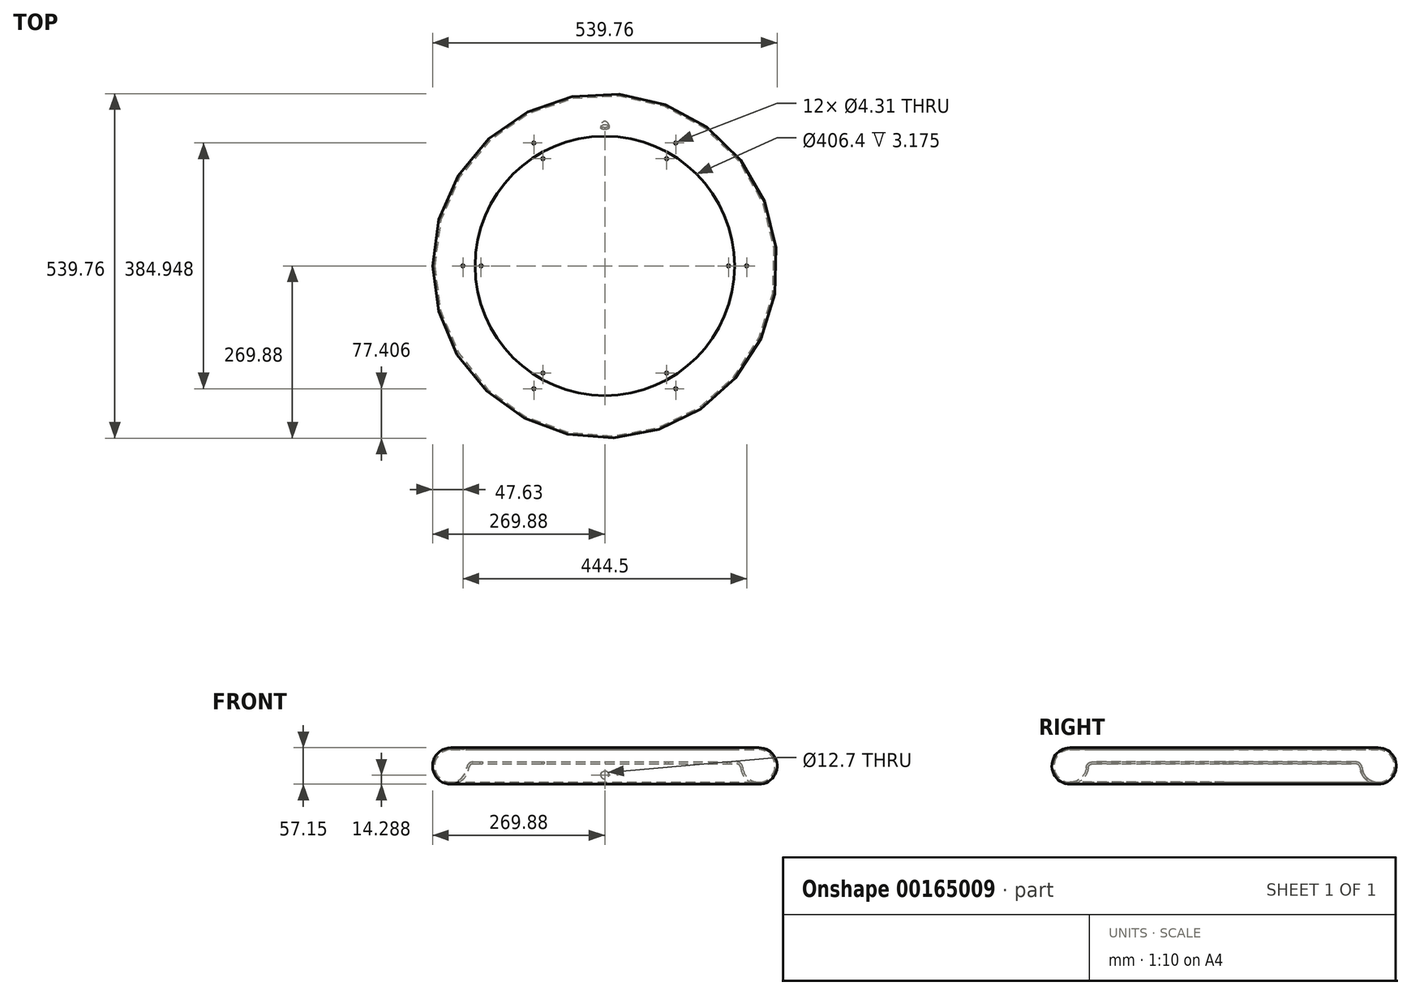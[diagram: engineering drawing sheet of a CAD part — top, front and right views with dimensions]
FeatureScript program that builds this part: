
annotation { "Feature Type Name" : "Feature", "Feature Type Description" : "" }
export const myFeature = defineFeature(function(context is Context, id is Id, definition is map)
    precondition{}
    {
        {
            var Q0;
            Q0=qCreatedBy(makeId("Front.planeOp"),FACE);
            var sketch = newSketch(context, id + "F0", { "sketchPlane" : qUnion([Q0])});
            skArc(sketch, "E0", {"start": v(212.84, -5.77) * mm, "mid": v(210.8, -1.66) * mm, "end": v(206.52, 0) * mm});
            skArc(sketch, "E1", {"start": v(216, -5.48) * mm, "mid": v(212.94, 0.68) * mm, "end": v(206.52, 3.17) * mm});
            skArc(sketch, "E2", {"start": v(212.84, -5.77) * mm, "mid": v(262.4, -22.44) * mm, "end": v(241.3, 25.4) * mm});
            skArc(sketch, "E3", {"start": v(216, -5.48) * mm, "mid": v(260.06, -20.3) * mm, "end": v(241.3, 22.23) * mm});
            skLineSegment(sketch, "E4.bottom", {"start": v(0, 0) * mm, "end": v(206.52, 0) * mm});
            skLineSegment(sketch, "E4.top", {"start": v(0, 3.18) * mm, "end": v(206.52, 3.18) * mm});
            skLineSegment(sketch, "E4.left", {"start": v(0, 0) * mm, "end": v(0, 3.18) * mm});
            skLineSegment(sketch, "E5", {"start": v(241.3, 22.23) * mm, "end": v(203.2, 22.23) * mm});
            skLineSegment(sketch, "E6", {"start": v(203.2, 22.23) * mm, "end": v(203.2, 25.4) * mm});
            skLineSegment(sketch, "E7", {"start": v(203.2, 25.4) * mm, "end": v(241.3, 25.4) * mm});
            skLineSegment(sketch, "E8", {"start": v(0, 3.18) * mm, "end": v(0, 22.23) * mm, "construction": true});
            skLineSegment(sketch, "E9", {"start": v(0, 22.23) * mm, "end": v(203.2, 22.23) * mm, "construction": true});
            skLineSegment(sketch, "E10", {"start": v(241.3, 25.4) * mm, "end": v(241.3, 69.85) * mm, "construction": true});
            skArc(sketch, "E11", {"start": v(212.87, -6.35) * mm, "mid": v(212.86, -6.06) * mm, "end": v(212.84, -5.77) * mm, "construction": true});
            skLineSegment(sketch, "E12", {"start": v(0, 0) * mm, "end": v(0, -6.35) * mm, "construction": true});
            skLineSegment(sketch, "E13", {"start": v(0, -6.35) * mm, "end": v(212.87, -6.35) * mm, "construction": true});
            skSolve(sketch);
        }
        {
            var Q0;
            Q0=qCreatedBy(makeId("Top.planeOp"),FACE);
            var sketch = newSketch(context, id + "F1", { "sketchPlane" : qUnion([Q0])});
            skCircle(sketch, "E14", {"center": v(0, 0) * mm, "radius": 25.4 * mm});
            skSolve(sketch);
        }
        {
            var Q0;
            Q0=qSketchRegion(id+"F0",true);
            var Q1;
            Q1=sQuery(id+"F1.wireOp",EDGE,"E14");
            revolve(context, id + "F2", {"entities" : qUnion([Q0]), "axis" : qUnion([Q1]), "revolveType" : RevolveType.FULL});
        }
        {
            var Q0;
            Q0=qCreatedBy(makeId("Front.planeOp"),FACE);
            var sketch = newSketch(context, id + "F3", { "sketchPlane" : qUnion([Q0])});
            skLineSegment(sketch, "E15", {"start": v(0, 3.18) * mm, "end": v(0, -17.46) * mm, "construction": true});
            skCircle(sketch, "E16", {"center": v(0, -17.46) * mm, "radius": 6.35 * mm});
            skSolve(sketch);
        }
        {
            var Q0;
            Q0=qSketchRegion(id+"F3",true);
            var Q1;
            Q1=makeQuery(id+"F2.opRevolve","SWEPT_FACE",FACE,{"disambiguationData":[OSD([sQuery(id+"F0.wireOp",EDGE,"E3")])]});
            extrude(context, id + "F4", {"entities" : qUnion([Q0]), "operationType" : NewBodyOperationType.REMOVE, "endBound" : BoundingType.UP_TO_SURFACE, "oppositeDirection" : true, "endBoundEntityFace" : qUnion([Q1]), "depth" : 25.4 * mm});
        }
        {
            var Q0;
            Q0=makeQuery(id+"F2.opRevolve","SWEPT_FACE",FACE,{"disambiguationData":[OSD([sQuery(id+"F0.wireOp",EDGE,"E4.bottom")])]});
            var sketch = newSketch(context, id + "F5", { "sketchPlane" : qUnion([Q0])});
            skCircle(sketch, "E17.cCircle", {"center": v(0, 0) * mm, "radius": 167.85 * mm, "construction": true});
            skLineSegment(sketch, "E17.0", {"start": v(-96.9, 167.85) * mm, "end": v(96.9, 167.85) * mm, "construction": true});
            skLineSegment(sketch, "E17.1", {"start": v(96.9, 167.85) * mm, "end": v(193.82, 0) * mm, "construction": true});
            skLineSegment(sketch, "E17.2", {"start": v(193.82, 0) * mm, "end": v(96.9, -167.85) * mm, "construction": true});
            skLineSegment(sketch, "E17.3", {"start": v(96.9, -167.85) * mm, "end": v(-96.9, -167.85) * mm, "construction": true});
            skLineSegment(sketch, "E17.4", {"start": v(-96.9, -167.85) * mm, "end": v(-193.82, 0) * mm, "construction": true});
            skLineSegment(sketch, "E17.5", {"start": v(-193.82, 0) * mm, "end": v(-96.9, 167.85) * mm, "construction": true});
            skPoint(sketch, "E17.0.midPoint", {"position": v(0, 167.85) * mm});
            skCircle(sketch, "E18", {"center": v(-96.9, 167.85) * mm, "radius": 12.7 * mm, "construction": true});
            skCircle(sketch, "E19", {"center": v(-96.9, 167.85) * mm, "radius": 2.15 * mm});
            skCircle(sketch, "E20", {"center": v(96.9, 167.85) * mm, "radius": 2.15 * mm});
            skCircle(sketch, "E21", {"center": v(193.82, 0) * mm, "radius": 2.15 * mm});
            skCircle(sketch, "E22", {"center": v(96.9, -167.85) * mm, "radius": 2.15 * mm});
            skCircle(sketch, "E23", {"center": v(-96.9, -167.85) * mm, "radius": 2.15 * mm});
            skCircle(sketch, "E24", {"center": v(-193.82, 0) * mm, "radius": 2.15 * mm});
            skSolve(sketch);
        }
        {
            var Q0;
            Q0=qSketchRegion(id+"F5",true);
            var Q1;
            Q1=makeQuery(id+"FbnNhXNbsYmOufx_1.boolean.opBoolean","SPLIT",FACE,{"disambiguationData":[TD([makeQuery(id+"F2.opRevolve","SWEPT_FACE",FACE,{"disambiguationData":[OSD([sQuery(id+"F0.wireOp",EDGE,"E1")])]})])],"derivedFrom":makeQuery(id+"F2.opRevolve","SWEPT_FACE",FACE,{"disambiguationData":[OSD([sQuery(id+"F0.wireOp",EDGE,"E4.top")])]})});
            extrude(context, id + "F6", {"entities" : qUnion([Q0]), "operationType" : NewBodyOperationType.REMOVE, "endBound" : BoundingType.UP_TO_SURFACE, "oppositeDirection" : true, "endBoundEntityFace" : qUnion([Q1]), "depth" : 25.4 * mm});
        }
        {
            var Q0;
            Q0=makeQuery(id+"F2.opRevolve","SWEPT_FACE",FACE,{"disambiguationData":[OSD([sQuery(id+"F0.wireOp",EDGE,"E7")])]});
            var sketch = newSketch(context, id + "F7", { "sketchPlane" : qUnion([Q0])});
            skCircle(sketch, "E25.cCircle", {"center": v(0, 0) * mm, "radius": 192.47 * mm, "construction": true});
            skLineSegment(sketch, "E25.0", {"start": v(-111.13, 192.47) * mm, "end": v(111.12, 192.47) * mm, "construction": true});
            skLineSegment(sketch, "E25.1", {"start": v(111.12, 192.47) * mm, "end": v(222.25, 0) * mm, "construction": true});
            skLineSegment(sketch, "E25.2", {"start": v(222.25, 0) * mm, "end": v(111.13, -192.47) * mm, "construction": true});
            skLineSegment(sketch, "E25.3", {"start": v(111.13, -192.47) * mm, "end": v(-111.12, -192.47) * mm, "construction": true});
            skLineSegment(sketch, "E25.4", {"start": v(-111.12, -192.47) * mm, "end": v(-222.25, 0) * mm, "construction": true});
            skLineSegment(sketch, "E25.5", {"start": v(-222.25, 0) * mm, "end": v(-111.13, 192.47) * mm, "construction": true});
            skCircle(sketch, "E26", {"center": v(111.12, 192.47) * mm, "radius": 19.05 * mm, "construction": true});
            skCircle(sketch, "E27", {"center": v(-111.13, 192.47) * mm, "radius": 2.15 * mm});
            skCircle(sketch, "E28", {"center": v(111.12, 192.47) * mm, "radius": 2.15 * mm});
            skCircle(sketch, "E29", {"center": v(222.25, 0) * mm, "radius": 2.15 * mm});
            skCircle(sketch, "E30", {"center": v(111.13, -192.47) * mm, "radius": 2.15 * mm});
            skCircle(sketch, "E31", {"center": v(-111.12, -192.47) * mm, "radius": 2.15 * mm});
            skCircle(sketch, "E32", {"center": v(-222.25, 0) * mm, "radius": 2.15 * mm});
            skSolve(sketch);
        }
        {
            var Q0;
            Q0 = qSketchRegion(id + "F7", true);
            var Q1;
            Q1=makeQuery(id+"FbnNhXNbsYmOufx_1.boolean.opBoolean","SPLIT",FACE,{"disambiguationData":[TD([makeQuery(id+"F2.opRevolve","SWEPT_FACE",FACE,{"disambiguationData":[OSD([sQuery(id+"F0.wireOp",EDGE,"E1")])]})])],"derivedFrom":makeQuery(id+"F2.opRevolve","SWEPT_FACE",FACE,{"disambiguationData":[OSD([sQuery(id+"F0.wireOp",EDGE,"E4.top")])]})});
            extrude(context, id + "F8", {"entities" : qUnion([Q0]), "operationType" : NewBodyOperationType.REMOVE, "endBound" : BoundingType.UP_TO_SURFACE, "oppositeDirection" : true, "endBoundEntityFace" : qUnion([Q1]), "depth" : 25.4 * mm});
        }
    });
